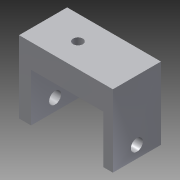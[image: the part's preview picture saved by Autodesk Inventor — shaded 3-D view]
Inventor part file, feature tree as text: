
AUTODESK INVENTOR PART (.ipt)
format: ipt  version: 2013 (Build 170138000, 138)  size: 98,304 bytes
history: native  units: in
note: dims shown in document units (in); Inventor stores cm internally (conversion verified against a paired STEP export)
features: extrude x3, sketch x3
ambient origin geometry x8: Origin, YZ Plane, XZ Plane, XY Plane, X Axis, Y Axis, Z Axis, Center Point
bodies: Solid1 (feature_tree)
feature tree (6):
  extrude  "Extrusion1"  Depth=0.75in
  extrude  "Extrusion2"  Depth=0.75in
  extrude  "Extrusion3"  Depth=0.5in TaperAngle=0.0deg
  sketch  "Sketch1"  dims[d0=0.5in d1=0.75in]
  sketch  "Sketch2"  dims[d2=0.125in d4=0.75in]
  sketch  "Sketch3"  dims[d5=0.975in d6=0.5in d7=0.0in d8=0.1015in d10=1.0in d11=0.0in d12=0.125in d14=0.125in d15=1.0in d16=0.0in]
